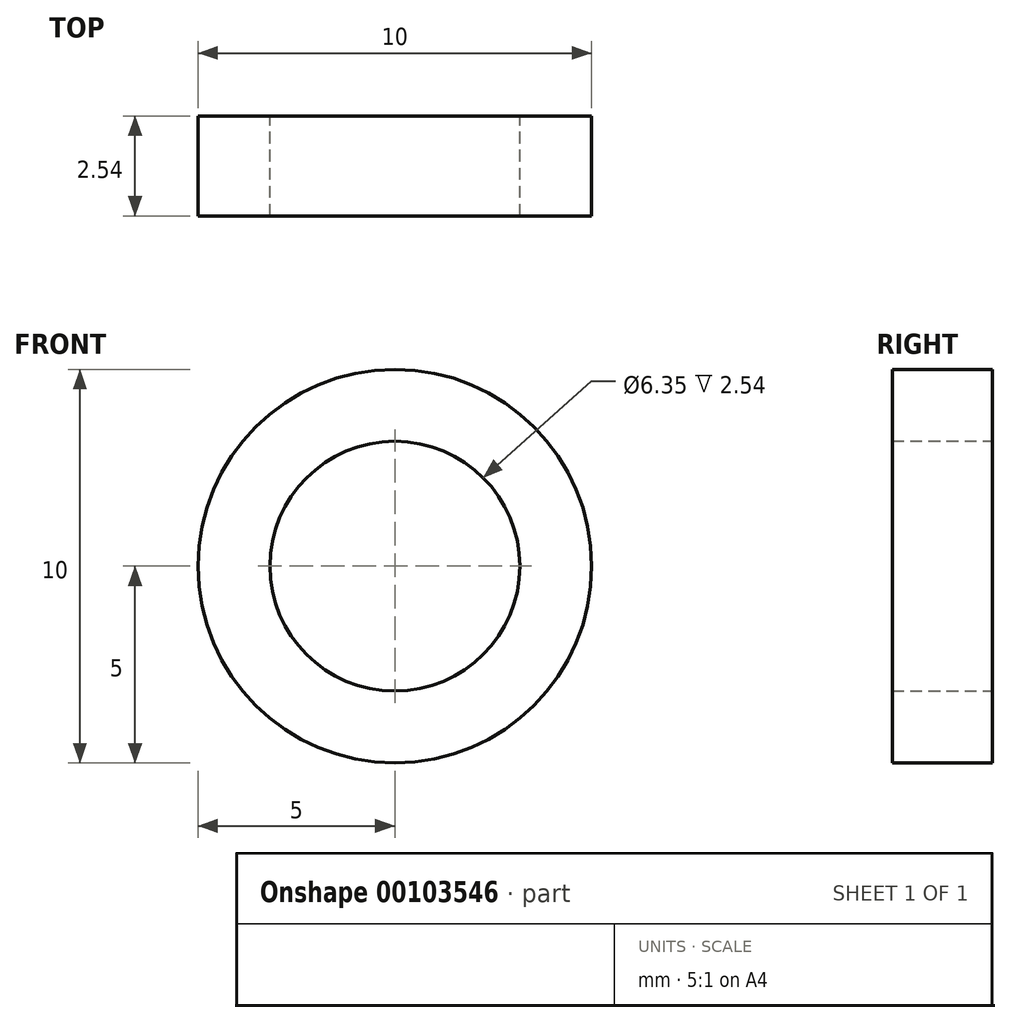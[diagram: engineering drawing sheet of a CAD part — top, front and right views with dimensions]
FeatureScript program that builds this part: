
annotation { "Feature Type Name" : "Feature", "Feature Type Description" : "" }
export const myFeature = defineFeature(function(context is Context, id is Id, definition is map)
    precondition{}
    {
        {
            var Q0;
            Q0=qCreatedBy(makeId("Front.planeOp"),FACE);
            var sketch = newSketch(context, id + "F0", { "sketchPlane" : qUnion([Q0])});
            skCircle(sketch, "E0", {"center": v(0, 0) * mm, "radius": 5 * mm});
            skCircle(sketch, "E1", {"center": v(0, 0) * mm, "radius": 3.18 * mm});
            skSolve(sketch);
        }
        {
            var Q0;
            Q0=makeQuery(id+"F0.imprint","IMPRINT",FACE,{"disambiguationData":[TD([[makeQuery(id+"F0.imprint","IMPRINT",EDGE,{"derivedFrom":sQuery(id+"F0.wireOp",EDGE,"E0")}),1.0]])]});
            extrude(context, id + "F1", {"entities" : qUnion([Q0]), "depth" : 2.54 * mm});
        }
    });
